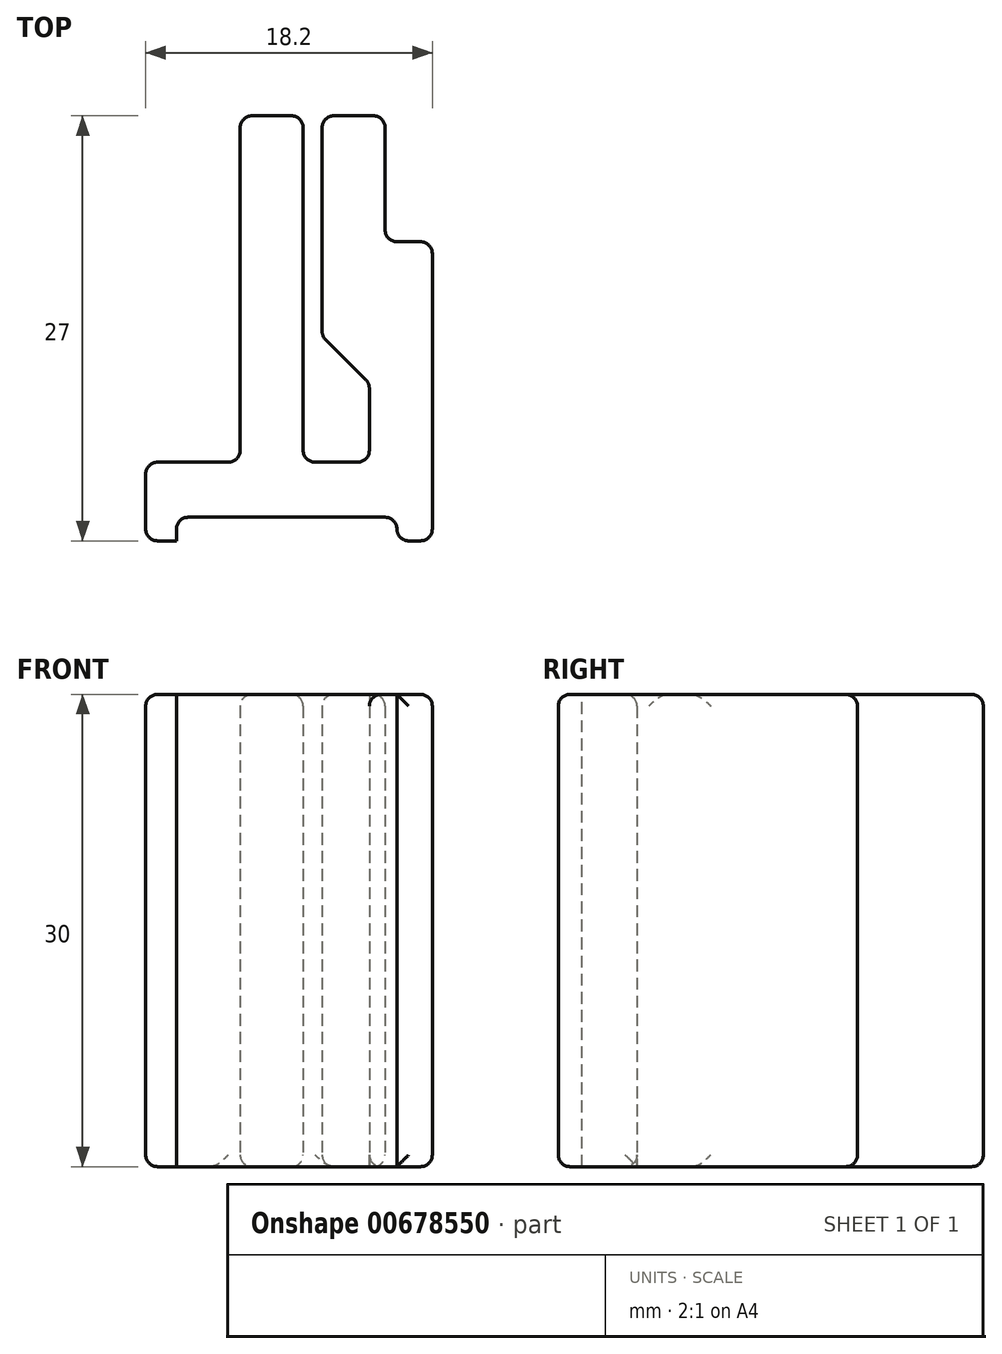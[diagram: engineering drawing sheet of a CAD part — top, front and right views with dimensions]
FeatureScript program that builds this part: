
annotation { "Feature Type Name" : "Feature", "Feature Type Description" : "" }
export const myFeature = defineFeature(function(context is Context, id is Id, definition is map)
    precondition{}
    {
        {
            var Q0;
            Q0=qCreatedBy(makeId("Top.planeOp"),FACE);
            var sketch = newSketch(context, id + "F0", { "sketchPlane" : qUnion([Q0])});
            skLineSegment(sketch, "E0", {"start": v(16, -8) * mm, "end": v(10, -8) * mm});
            skLineSegment(sketch, "E1", {"start": v(10, -8) * mm, "end": v(10, -13) * mm});
            skLineSegment(sketch, "E2", {"start": v(10, -13) * mm, "end": v(28.2, -13) * mm});
            skLineSegment(sketch, "E3", {"start": v(28.2, -13) * mm, "end": v(28.2, 6) * mm});
            skLineSegment(sketch, "E4", {"start": v(25.2, 14) * mm, "end": v(21.2, 14) * mm});
            skLineSegment(sketch, "E5", {"start": v(21.2, 14) * mm, "end": v(21.2, 0) * mm});
            skLineSegment(sketch, "E6", {"start": v(24.2, -8) * mm, "end": v(20, -8) * mm});
            skLineSegment(sketch, "E7", {"start": v(20, -8) * mm, "end": v(20, 14) * mm});
            skLineSegment(sketch, "E8", {"start": v(20, 14) * mm, "end": v(16, 14) * mm});
            skLineSegment(sketch, "E9", {"start": v(16, 14) * mm, "end": v(16, -8) * mm});
            skLineSegment(sketch, "E10", {"start": v(25.2, 6) * mm, "end": v(25.2, 14) * mm});
            skLineSegment(sketch, "E11", {"start": v(25.2, 6) * mm, "end": v(28.2, 6) * mm});
            skLineSegment(sketch, "E12", {"start": v(24.2, -8) * mm, "end": v(24.2, -3) * mm});
            skLineSegment(sketch, "E13", {"start": v(24.2, -3) * mm, "end": v(21.2, 0) * mm});
            skSolve(sketch);
        }
        {
            var Q0;
            Q0=makeQuery(id+"F0.imprint","IMPRINT",FACE,{"disambiguationData":[TD([[makeQuery(id+"F0.imprint","IMPRINT",EDGE,{"derivedFrom":sQuery(id+"F0.wireOp",EDGE,"E0")}),1.0]])]});
            extrude(context, id + "F1", {"entities" : qUnion([Q0]), "depth" : 30 * mm, "offsetDistance" : 25 * mm});
        }
        {
            var Q0;
            Q0=makeQuery(id+"F1.opExtrude","SWEPT_FACE",FACE,{"disambiguationData":[OSD([sQuery(id+"F0.wireOp",EDGE,"E2")])]});
            var sketch = newSketch(context, id + "F2", { "sketchPlane" : qUnion([Q0])});
            skLineSegment(sketch, "E14.bottom", {"start": v(11.95, 0) * mm, "end": v(25.95, 0) * mm});
            skLineSegment(sketch, "E14.top", {"start": v(11.95, 30) * mm, "end": v(25.95, 30) * mm});
            skLineSegment(sketch, "E14.left", {"start": v(11.95, 0) * mm, "end": v(11.95, 30) * mm});
            skLineSegment(sketch, "E14.right", {"start": v(25.95, 0) * mm, "end": v(25.95, 30) * mm});
            skSolve(sketch);
        }
        {
            var Q0;
            Q0 = qSketchRegion(id + "F2", true);
            extrude(context, id + "F3", {"entities" : qUnion([Q0]), "operationType" : NewBodyOperationType.REMOVE, "oppositeDirection" : true, "depth" : 1.5 * mm, "offsetDistance" : 25 * mm});
        }
        {
            var Q0;
            Q0=makeQuery(id+"F1.opExtrude","SWEPT_EDGE",EDGE,{"disambiguationData":[OSD([sQuery(id+"F0.wireOp",EDGE,"E4"),sQuery(id+"F0.wireOp",EDGE,"E5")])]});
            var Q1;
            Q1=makeQuery(id+"F1.opExtrude","SWEPT_EDGE",EDGE,{"disambiguationData":[OSD([sQuery(id+"F0.wireOp",EDGE,"E0"),sQuery(id+"F0.wireOp",EDGE,"E1")])]});
            var Q2;
            Q2=makeQuery(id+"F1.opExtrude","CAP_EDGE",EDGE,{"disambiguationData":[OSD([sQuery(id+"F0.wireOp",EDGE,"E1")])],"isStart":false});
            var Q3;
            Q3=makeQuery(id+"F1.opExtrude","CAP_EDGE",EDGE,{"disambiguationData":[OSD([sQuery(id+"F0.wireOp",EDGE,"E1")])],"isStart":true});
            var Q4;
            Q4=makeQuery(id+"F1.opExtrude","CAP_EDGE",EDGE,{"disambiguationData":[OSD([sQuery(id+"F0.wireOp",EDGE,"E0")])],"isStart":false});
            var Q5;
            Q5=makeQuery(id+"F1.opExtrude","CAP_EDGE",EDGE,{"disambiguationData":[OSD([sQuery(id+"F0.wireOp",EDGE,"E9")])],"isStart":false});
            var Q6;
            Q6=makeQuery(id+"F1.opExtrude","SWEPT_EDGE",EDGE,{"disambiguationData":[OSD([sQuery(id+"F0.wireOp",EDGE,"E8"),sQuery(id+"F0.wireOp",EDGE,"E9")])]});
            var Q7;
            Q7=makeQuery(id+"F1.opExtrude","CAP_EDGE",EDGE,{"disambiguationData":[OSD([sQuery(id+"F0.wireOp",EDGE,"E9")])],"isStart":true});
            var Q8;
            Q8=makeQuery(id+"F1.opExtrude","SWEPT_EDGE",EDGE,{"disambiguationData":[OSD([sQuery(id+"F0.wireOp",EDGE,"E0"),sQuery(id+"F0.wireOp",EDGE,"E9")])]});
            var Q9;
            Q9=makeQuery(id+"F1.opExtrude","CAP_EDGE",EDGE,{"disambiguationData":[OSD([sQuery(id+"F0.wireOp",EDGE,"E4")])],"isStart":true});
            var Q10;
            Q10=makeQuery(id+"F1.opExtrude","SWEPT_EDGE",EDGE,{"disambiguationData":[OSD([sQuery(id+"F0.wireOp",EDGE,"E7"),sQuery(id+"F0.wireOp",EDGE,"E8")])]});
            var Q11;
            Q11=makeQuery(id+"F1.opExtrude","CAP_EDGE",EDGE,{"disambiguationData":[OSD([sQuery(id+"F0.wireOp",EDGE,"E7")])],"isStart":false});
            var Q12;
            Q12=makeQuery(id+"F1.opExtrude","CAP_EDGE",EDGE,{"disambiguationData":[OSD([sQuery(id+"F0.wireOp",EDGE,"E5")])],"isStart":false});
            var Q13;
            Q13=makeQuery(id+"F1.opExtrude","CAP_EDGE",EDGE,{"disambiguationData":[OSD([sQuery(id+"F0.wireOp",EDGE,"E6")])],"isStart":false});
            var Q14;
            Q14=makeQuery(id+"F1.opExtrude","SWEPT_EDGE",EDGE,{"disambiguationData":[OSD([sQuery(id+"F0.wireOp",EDGE,"E6"),sQuery(id+"F0.wireOp",EDGE,"E12")])]});
            var Q15;
            Q15=makeQuery(id+"F1.opExtrude","SWEPT_EDGE",EDGE,{"disambiguationData":[OSD([sQuery(id+"F0.wireOp",EDGE,"E6"),sQuery(id+"F0.wireOp",EDGE,"E7")])]});
            var Q16;
            Q16=makeQuery(id+"F1.opExtrude","CAP_EDGE",EDGE,{"disambiguationData":[OSD([sQuery(id+"F0.wireOp",EDGE,"E5")])],"isStart":true});
            var Q17;
            Q17=makeQuery(id+"F1.opExtrude","CAP_EDGE",EDGE,{"disambiguationData":[OSD([sQuery(id+"F0.wireOp",EDGE,"E7")])],"isStart":true});
            var Q18;
            Q18=makeQuery(id+"F1.opExtrude","CAP_EDGE",EDGE,{"disambiguationData":[OSD([sQuery(id+"F0.wireOp",EDGE,"E4")])],"isStart":false});
            var Q19;
            Q19=makeQuery(id+"F1.opExtrude","CAP_EDGE",EDGE,{"disambiguationData":[OSD([sQuery(id+"F0.wireOp",EDGE,"E8")])],"isStart":false});
            var Q20;
            Q20=makeQuery(id+"F1.opExtrude","CAP_EDGE",EDGE,{"disambiguationData":[OSD([sQuery(id+"F0.wireOp",EDGE,"E8")])],"isStart":true});
            var Q21;
            Q21=makeQuery(id+"F1.opExtrude","SWEPT_EDGE",EDGE,{"disambiguationData":[OSD([sQuery(id+"F0.wireOp",EDGE,"E1"),sQuery(id+"F0.wireOp",EDGE,"E2")])]});
            var Q22;
            Q22=makeQuery(id+"F3.boolean.opBoolean","COPY",EDGE,{"derivedFrom":makeQuery(id+"F3.opExtrude","CAP_EDGE",EDGE,{"disambiguationData":[OSD([sQuery(id+"F2.wireOp",EDGE,"E14.left")])],"isStart":true})});
            var Q23;
            Q23=makeQuery(id+"F3.boolean.opBoolean","COPY",EDGE,{"derivedFrom":makeQuery(id+"F3.opExtrude","CAP_EDGE",EDGE,{"disambiguationData":[OSD([sQuery(id+"F2.wireOp",EDGE,"E14.top")])],"isStart":false})});
            var Q24;
            Q24=makeQuery(id+"F1.opExtrude","SWEPT_EDGE",EDGE,{"disambiguationData":[OSD([sQuery(id+"F0.wireOp",EDGE,"E2"),sQuery(id+"F0.wireOp",EDGE,"E3")])]});
            var Q25;
            Q25=makeQuery(id+"F1.opExtrude","CAP_EDGE",EDGE,{"disambiguationData":[OSD([sQuery(id+"F0.wireOp",EDGE,"E3")])],"isStart":false});
            var Q26;
            Q26=makeQuery(id+"F3.boolean.opBoolean","COPY",EDGE,{"derivedFrom":makeQuery(id+"F3.opExtrude","CAP_EDGE",EDGE,{"disambiguationData":[OSD([sQuery(id+"F2.wireOp",EDGE,"E14.right")])],"isStart":true})});
            var Q27;
            Q27=makeQuery(id+"F3.boolean.opBoolean","COPY",EDGE,{"derivedFrom":makeQuery(id+"F3.opExtrude","CAP_EDGE",EDGE,{"disambiguationData":[OSD([sQuery(id+"F2.wireOp",EDGE,"E14.bottom")])],"isStart":false})});
            var Q28;
            Q28=makeQuery(id+"F1.opExtrude","CAP_EDGE",EDGE,{"disambiguationData":[OSD([sQuery(id+"F0.wireOp",EDGE,"E3")])],"isStart":true});
            var Q29;
            Q29=makeQuery(id+"F3.boolean.opBoolean","COPY",EDGE,{"derivedFrom":makeQuery(id+"F3.opExtrude","SWEPT_EDGE",EDGE,{"disambiguationData":[OSD([sQuery(id+"F0.wireOp",EDGE,"E2"),sQuery(id+"F2.wireOp",EDGE,"E14.bottom"),sQuery(id+"F2.wireOp",EDGE,"E14.right")])]})});
            var Q30;
            Q30=makeQuery(id+"F3.boolean.opBoolean","COPY",EDGE,{"derivedFrom":makeQuery(id+"F3.opExtrude","CAP_EDGE",EDGE,{"disambiguationData":[OSD([sQuery(id+"F2.wireOp",EDGE,"E14.right")])],"isStart":false})});
            var Q31;
            Q31=makeQuery(id+"F3.boolean.opBoolean","COPY",EDGE,{"derivedFrom":makeQuery(id+"F3.opExtrude","SWEPT_EDGE",EDGE,{"disambiguationData":[OSD([sQuery(id+"F0.wireOp",EDGE,"E2"),sQuery(id+"F2.wireOp",EDGE,"E14.top"),sQuery(id+"F2.wireOp",EDGE,"E14.right")])]})});
            var Q32;
            Q32=makeQuery(id+"F3.boolean.opBoolean","COPY",EDGE,{"derivedFrom":makeQuery(id+"F3.opExtrude","SWEPT_EDGE",EDGE,{"disambiguationData":[OSD([sQuery(id+"F0.wireOp",EDGE,"E2"),sQuery(id+"F2.wireOp",EDGE,"E14.top"),sQuery(id+"F2.wireOp",EDGE,"E14.left")])]})});
            var Q33;
            Q33=makeQuery(id+"F3.boolean.opBoolean","COPY",EDGE,{"derivedFrom":makeQuery(id+"F3.opExtrude","SWEPT_EDGE",EDGE,{"disambiguationData":[OSD([sQuery(id+"F0.wireOp",EDGE,"E2"),sQuery(id+"F2.wireOp",EDGE,"E14.bottom"),sQuery(id+"F2.wireOp",EDGE,"E14.left")])]})});
            var Q34;
            {var subQ0=sQuery(id+"F0.wireOp",EDGE,"E2");var subQ1=sQuery(id+"F0.wireOp",EDGE,"E1");Q34=makeQuery(id+"F3.boolean.opBoolean","SPLIT",EDGE,{"disambiguationData":[TD([makeQuery(id+"F1.opExtrude","SWEPT_FACE",FACE,{"disambiguationData":[OSD([subQ1])]})])],"derivedFrom":makeQuery(id+"F1.opExtrude","CAP_EDGE",EDGE,{"disambiguationData":[OSD([subQ0])],"isStart":true})});}
            var Q35;
            {var subQ0=sQuery(id+"F0.wireOp",EDGE,"E2");var subQ1=sQuery(id+"F0.wireOp",EDGE,"E1");Q35=makeQuery(id+"F3.boolean.opBoolean","SPLIT",EDGE,{"disambiguationData":[TD([makeQuery(id+"F1.opExtrude","SWEPT_FACE",FACE,{"disambiguationData":[OSD([subQ1])]})])],"derivedFrom":makeQuery(id+"F1.opExtrude","CAP_EDGE",EDGE,{"disambiguationData":[OSD([subQ0])],"isStart":false})});}
            var Q36;
            Q36=makeQuery(id+"F3.boolean.opBoolean","COPY",EDGE,{"derivedFrom":makeQuery(id+"F3.opExtrude","CAP_EDGE",EDGE,{"disambiguationData":[OSD([sQuery(id+"F2.wireOp",EDGE,"E14.left")])],"isStart":false})});
            var Q37;
            {var subQ0=sQuery(id+"F0.wireOp",EDGE,"E3");var subQ1=sQuery(id+"F0.wireOp",EDGE,"E2");Q37=makeQuery(id+"F3.boolean.opBoolean","SPLIT",EDGE,{"disambiguationData":[TD([makeQuery(id+"F1.opExtrude","SWEPT_FACE",FACE,{"disambiguationData":[OSD([subQ0])]})])],"derivedFrom":makeQuery(id+"F1.opExtrude","CAP_EDGE",EDGE,{"disambiguationData":[OSD([subQ1])],"isStart":false})});}
            var Q38;
            {var subQ0=sQuery(id+"F0.wireOp",EDGE,"E3");var subQ1=sQuery(id+"F0.wireOp",EDGE,"E2");Q38=makeQuery(id+"F3.boolean.opBoolean","SPLIT",EDGE,{"disambiguationData":[TD([makeQuery(id+"F1.opExtrude","SWEPT_FACE",FACE,{"disambiguationData":[OSD([subQ0])]})])],"derivedFrom":makeQuery(id+"F1.opExtrude","CAP_EDGE",EDGE,{"disambiguationData":[OSD([subQ1])],"isStart":true})});}
            var Q39;
            Q39=makeQuery(id+"F1.opExtrude","SWEPT_EDGE",EDGE,{"disambiguationData":[OSD([sQuery(id+"F0.wireOp",EDGE,"E3"),sQuery(id+"F0.wireOp",EDGE,"E11")])]});
            var Q40;
            Q40=makeQuery(id+"F1.opExtrude","SWEPT_EDGE",EDGE,{"disambiguationData":[OSD([sQuery(id+"F0.wireOp",EDGE,"E4"),sQuery(id+"F0.wireOp",EDGE,"E10")])]});
            var Q41;
            Q41=makeQuery(id+"F1.opExtrude","SWEPT_EDGE",EDGE,{"disambiguationData":[OSD([sQuery(id+"F0.wireOp",EDGE,"E10"),sQuery(id+"F0.wireOp",EDGE,"E11")])]});
            var Q42;
            Q42=makeQuery(id+"F1.opExtrude","CAP_EDGE",EDGE,{"disambiguationData":[OSD([sQuery(id+"F0.wireOp",EDGE,"E10")])],"isStart":false});
            var Q43;
            Q43=makeQuery(id+"F1.opExtrude","CAP_EDGE",EDGE,{"disambiguationData":[OSD([sQuery(id+"F0.wireOp",EDGE,"E11")])],"isStart":false});
            var Q44;
            Q44=makeQuery(id+"F1.opExtrude","CAP_EDGE",EDGE,{"disambiguationData":[OSD([sQuery(id+"F0.wireOp",EDGE,"E11")])],"isStart":true});
            var Q45;
            Q45=makeQuery(id+"F1.opExtrude","CAP_EDGE",EDGE,{"disambiguationData":[OSD([sQuery(id+"F0.wireOp",EDGE,"E10")])],"isStart":true});
            var Q46;
            Q46=makeQuery(id+"F1.opExtrude","SWEPT_FACE",FACE,{"disambiguationData":[OSD([sQuery(id+"F0.wireOp",EDGE,"E13")])]});
            fillet(context, id + "F4", {"entities" : qUnion([Q0, Q1, Q2, Q3, Q4, Q5, Q6, Q7, Q8, Q9, Q10, Q11, Q12, Q13, Q14, Q15, Q16, Q17, Q18, Q19, Q20, Q21, Q22, Q23, Q24, Q25, Q26, Q27, Q28, Q29, Q30, Q31, Q32, Q33, Q34, Q35, Q36, Q37, Q38, Q39, Q40, Q41, Q42, Q43, Q44, Q45, Q46]), "radius" : 0.75 * mm, "tangentPropagation" : true, "allowEdgeOverflow" : false});
        }
    });
